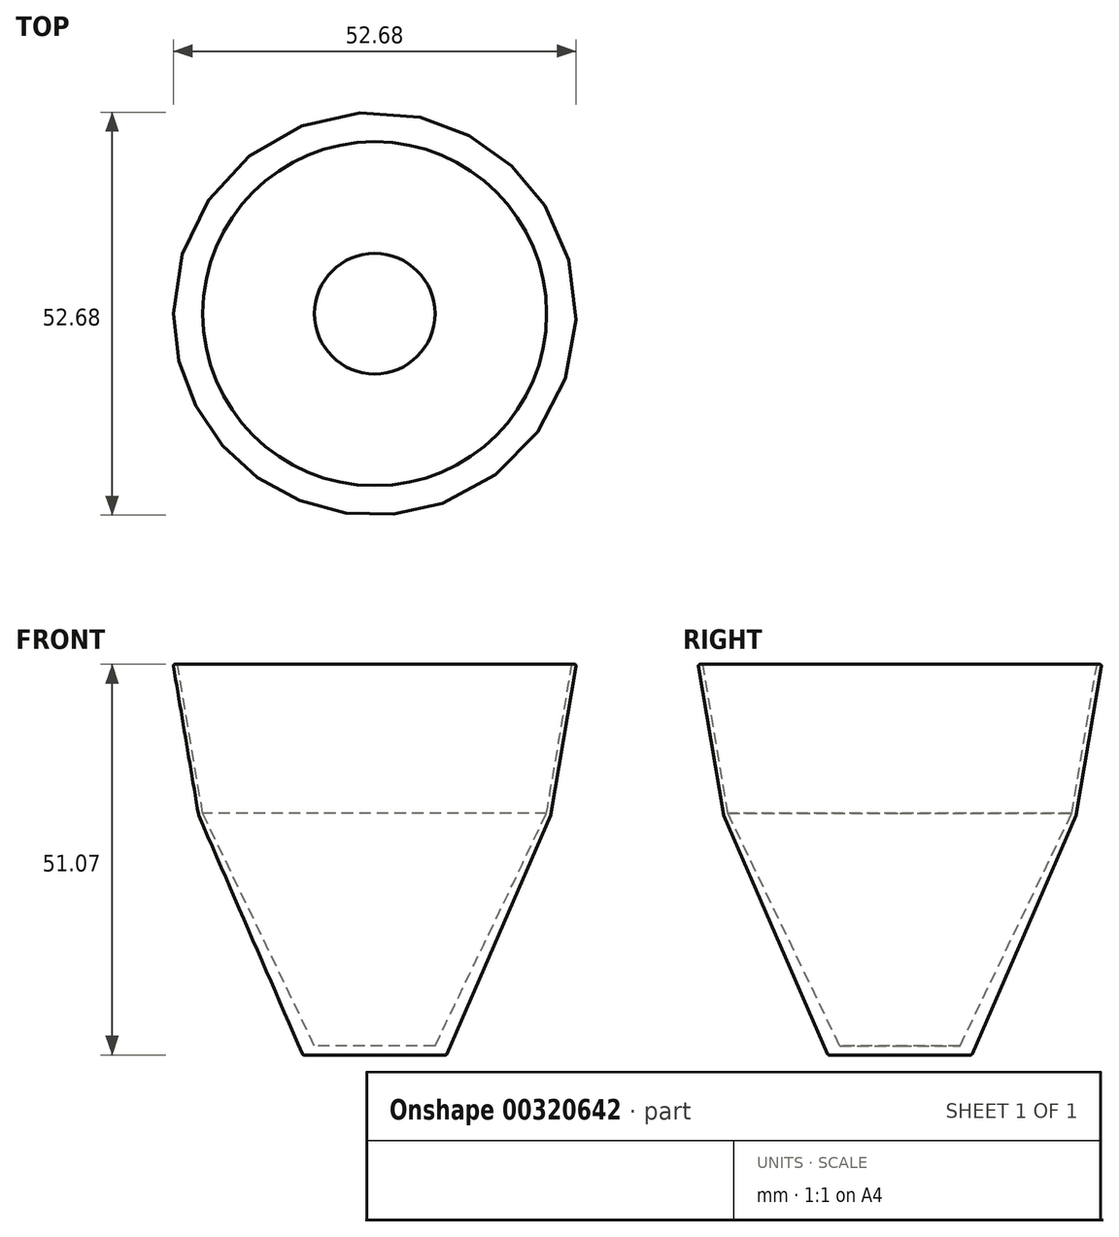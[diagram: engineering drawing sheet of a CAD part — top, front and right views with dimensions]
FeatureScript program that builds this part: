
annotation { "Feature Type Name" : "Feature", "Feature Type Description" : "" }
export const myFeature = defineFeature(function(context is Context, id is Id, definition is map)
    precondition{}
    {
        {
            var Q0;
            Q0=qCreatedBy(makeId("Front.planeOp"),FACE);
            var sketch = newSketch(context, id + "F0", { "sketchPlane" : qUnion([Q0])});
            skLineSegment(sketch, "E0", {"start": v(0, 0) * mm, "end": v(-9.4, 0) * mm});
            skLineSegment(sketch, "E1", {"start": v(-9.4, 0) * mm, "end": v(-23.04, 31.36) * mm});
            skLineSegment(sketch, "E2", {"start": v(-23.04, 31.36) * mm, "end": v(-26.37, 51.07) * mm});
            skLineSegment(sketch, "E3", {"start": v(-26.37, 51.07) * mm, "end": v(-25.78, 51.07) * mm});
            skLineSegment(sketch, "E4", {"start": v(-25.78, 51.07) * mm, "end": v(-22.48, 31.58) * mm});
            skLineSegment(sketch, "E5", {"start": v(-22.48, 31.58) * mm, "end": v(-7.88, 1.2) * mm});
            skLineSegment(sketch, "E6", {"start": v(-7.88, 1.2) * mm, "end": v(0, 1.2) * mm});
            skLineSegment(sketch, "E7", {"start": v(0, 1.2) * mm, "end": v(0, 0) * mm});
            skLineSegment(sketch, "E8", {"start": v(0, 1.2) * mm, "end": v(-3.66, 51.07) * mm, "construction": true});
            skSolve(sketch);
        }
        {
            var Q0;
            Q0=makeQuery(id+"F0.imprint","IMPRINT",FACE,{"disambiguationData":[TD([[makeQuery(id+"F0.imprint","IMPRINT",EDGE,{"derivedFrom":sQuery(id+"F0.wireOp",EDGE,"E0")}),-1.0]])]});
            var Q1;
            Q1=sQuery(id+"F0.wireOp",EDGE,"E7");
            revolve(context, id + "F1", {"entities" : qUnion([Q0]), "axis" : qUnion([Q1]), "revolveType" : RevolveType.FULL});
        }
        {
            var Q0;
            Q0=makeQuery(id+"F1.opRevolve","SWEPT_EDGE",EDGE,{"disambiguationData":[OSD([sQuery(id+"F0.wireOp",EDGE,"E1"),sQuery(id+"F0.wireOp",EDGE,"E2")])]});
            var Q1;
            Q1=makeQuery(id+"F1.opRevolve","SWEPT_EDGE",EDGE,{"disambiguationData":[OSD([sQuery(id+"F0.wireOp",EDGE,"E2"),sQuery(id+"F0.wireOp",EDGE,"E3")])]});
            var Q2;
            Q2=makeQuery(id+"F1.opRevolve","SWEPT_EDGE",EDGE,{"disambiguationData":[OSD([sQuery(id+"F0.wireOp",EDGE,"E0"),sQuery(id+"F0.wireOp",EDGE,"E1")])]});
            var Q3;
            Q3=makeQuery(id+"F1.opRevolve","SWEPT_EDGE",EDGE,{"disambiguationData":[OSD([sQuery(id+"F0.wireOp",EDGE,"E3"),sQuery(id+"F0.wireOp",EDGE,"E4")])]});
            fillet(context, id + "F2", {"entities" : qUnion([Q0, Q1, Q2, Q3]), "radius" : 0.2 * mm, "tangentPropagation" : true, "allowEdgeOverflow" : false});
        }
    });
